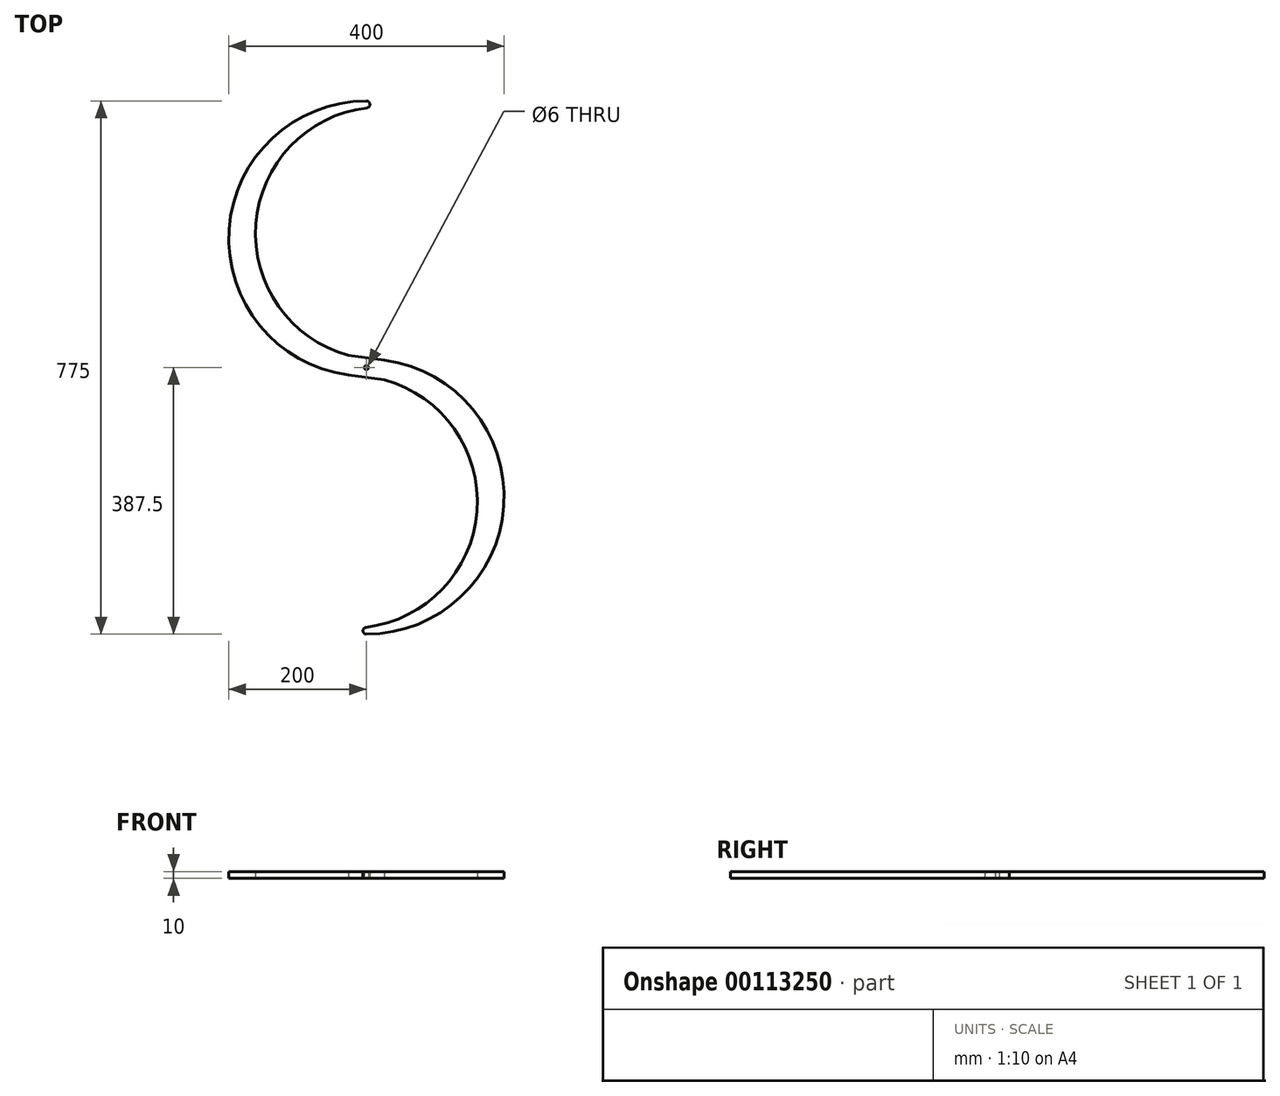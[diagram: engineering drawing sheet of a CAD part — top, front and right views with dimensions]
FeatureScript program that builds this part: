
annotation { "Feature Type Name" : "Feature", "Feature Type Description" : "" }
export const myFeature = defineFeature(function(context is Context, id is Id, definition is map)
    precondition{}
    {
        {
            var Q0;
            Q0=qCreatedBy(makeId("Top.planeOp"),FACE);
            var sketch = newSketch(context, id + "F0", { "sketchPlane" : qUnion([Q0])});
            skArc(sketch, "E0", {"start": v(0, 400) * mm, "mid": v(-199.57, 213.17) * mm, "end": v(-26.3, 1.74) * mm});
            skArc(sketch, "E1.0", {"start": v(0, 360) * mm, "mid": v(-160, 200) * mm, "end": v(0, 40) * mm, "construction": true});
            skLineSegment(sketch, "E2", {"start": v(0, 400) * mm, "end": v(0, 0) * mm, "construction": true});
            skLineSegment(sketch, "E3", {"start": v(0, 200) * mm, "end": v(-200, 200) * mm, "construction": true});
            skArc(sketch, "E4", {"start": v(0.6, 390.04) * mm, "mid": v(5, 395.3) * mm, "end": v(0, 400) * mm});
            skArc(sketch, "E5", {"start": v(0.6, 390.04) * mm, "mid": v(-160.7, 221.19) * mm, "end": v(-26.3, 30.24) * mm});
            skLineSegment(sketch, "E6", {"start": v(-180, 0) * mm, "end": v(-180, 107.7) * mm, "construction": true});
            skLineSegment(sketch, "E7", {"start": v(0, 25) * mm, "end": v(0, 0) * mm, "construction": true});
            skArc(sketch, "E8.1.0", {"start": v(0, -375) * mm, "mid": v(199.57, -188.17) * mm, "end": v(26.3, 23.26) * mm});
            skArc(sketch, "E8.1.1", {"start": v(-0.6, -365.04) * mm, "mid": v(160.7, -196.19) * mm, "end": v(26.3, -5.24) * mm});
            skArc(sketch, "E8.1.2", {"start": v(-0.6, -365.04) * mm, "mid": v(-5, -370.3) * mm, "end": v(0, -375) * mm});
            skPoint(sketch, "E8.center", {"position": v(0, 12.5) * mm});
            skCircle(sketch, "E9", {"center": v(0, 12.5) * mm, "radius": 3 * mm});
            skLineSegment(sketch, "E10", {"start": v(-26.3, 30.24) * mm, "end": v(26.3, 23.26) * mm});
            skPoint(sketch, "E11", {"position": v(0, 26.75) * mm});
            skLineSegment(sketch, "E12", {"start": v(-26.3, 1.74) * mm, "end": v(26.3, -5.24) * mm});
            skPoint(sketch, "E13", {"position": v(0, -1.75) * mm});
            skPoint(sketch, "E14.orphan", {"position": v(0, 25) * mm});
            skPoint(sketch, "E15.orphan", {"position": v(0, 0) * mm});
            skSolve(sketch);
        }
        {
            var Q0;
            Q0 = qSketchRegion(id + "F0", true);
            extrude(context, id + "F1", {"entities" : qUnion([Q0]), "depth" : 10 * mm});
        }
    });
